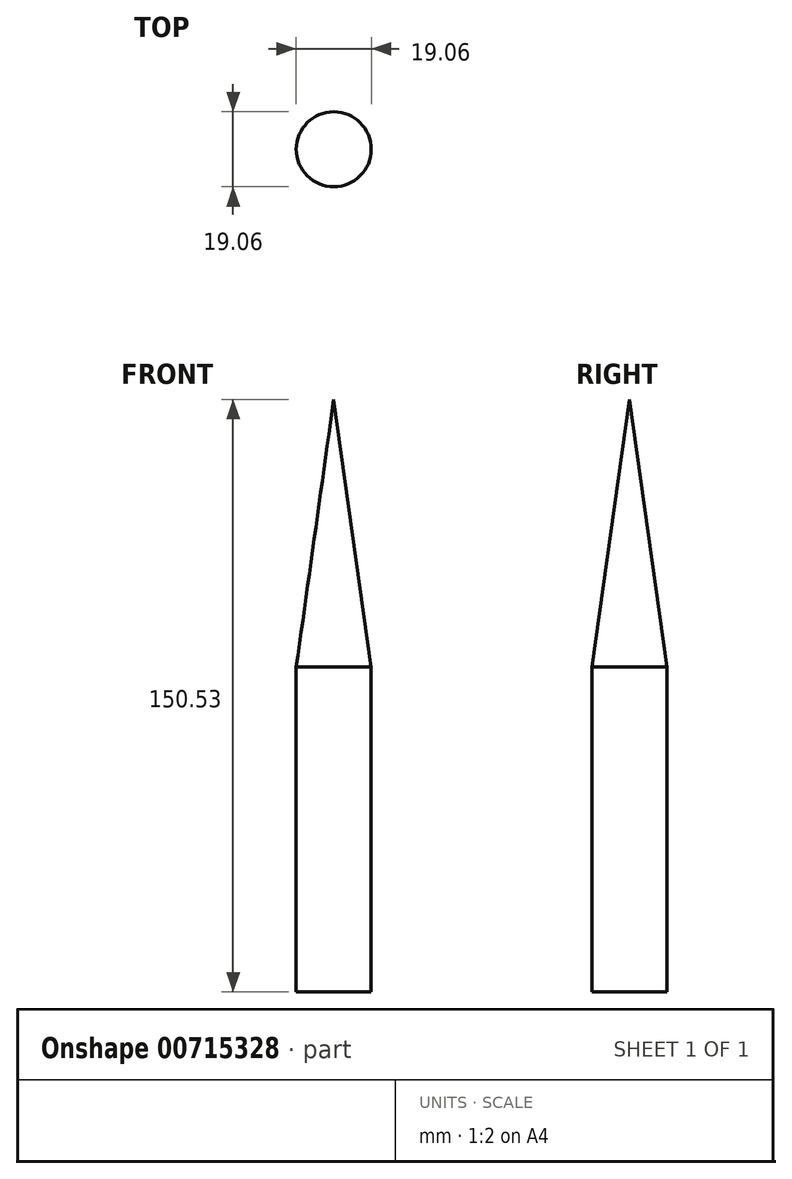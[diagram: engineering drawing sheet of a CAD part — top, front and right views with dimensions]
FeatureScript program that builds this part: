
annotation { "Feature Type Name" : "Feature", "Feature Type Description" : "" }
export const myFeature = defineFeature(function(context is Context, id is Id, definition is map)
    precondition{}
    {
        {
            var Q0;
            Q0=qCreatedBy(makeId("Right.planeOp"),FACE);
            var sketch = newSketch(context, id + "F0", { "sketchPlane" : qUnion([Q0])});
            skLineSegment(sketch, "E0", {"start": v(0, 0) * mm, "end": v(9.53, 0) * mm});
            skLineSegment(sketch, "E1", {"start": v(9.53, 0) * mm, "end": v(9.53, 82.55) * mm});
            skLineSegment(sketch, "E2", {"start": v(9.53, 82.55) * mm, "end": v(0, 150.53) * mm});
            skLineSegment(sketch, "E3", {"start": v(0, 150.53) * mm, "end": v(0, 0) * mm});
            skSolve(sketch);
        }
        {
            var Q0;
            Q0=makeQuery(id+"F0.imprint","IMPRINT",FACE,{"disambiguationData":[TD([[makeQuery(id+"F0.imprint","IMPRINT",EDGE,{"derivedFrom":sQuery(id+"F0.wireOp",EDGE,"E0")}),1.0]])]});
            var Q1;
            Q1=sQuery(id+"F0.wireOp",EDGE,"E3");
            revolve(context, id + "F1", {"surfaceOperationType" : NewSurfaceOperationType.NEW, "entities" : qUnion([Q0]), "axis" : qUnion([Q1]), "revolveType" : RevolveType.FULL});
        }
    });
